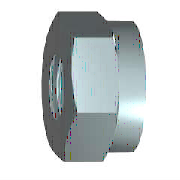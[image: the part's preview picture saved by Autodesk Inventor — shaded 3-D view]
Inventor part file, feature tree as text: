
AUTODESK INVENTOR PART (.ipt)
format: ipt  version: 2015 (Build 190159000, 159)  size: 194,048 bytes
history: native  units: mm (DEFAULTED — no unit token found)
features: sketch x4, extrude x1, chamfer x1, hole x1, other x1, plane x1, fillet x1
ambient origin geometry x7: Origin, YZ Plane, XZ Plane, X Axis, Y Axis, Z Axis, Center Point
bodies: Solid1 (feature_tree), Body (feature_tree)
feature tree (10):
  extrude  "Ring"  Depth=4.4mm
  chamfer  "Chamfer1"  Distance=6.88mm
  hole  "Thread"  [1 undecoded]
  other  "Work Axis1"
  plane  "Work Plane1"
  fillet  "Fillet1"  [1 undecoded]
  sketch  "Sketch1"  dims[d0=9.237604mm d1=4.4mm]
  sketch  "Sketch3"  dims[d3=30.0deg]
  sketch  "Sketch2"  dims[d2=0.0mm]
  sketch  "Sketch4"  dims[d4=30.0deg d5=6.88mm d6=6.88mm d26=90.0deg d7=6.88mm d8=2.4mm d9=0.0mm d30=4.134mm d31=6.0mm d32=4.0mm d33=2.0mm d34=14.3117mm d35=8.0mm d36=20.594885mm d10=0.433013mm d11=30.0deg d12=0.433013mm d13=30.0deg d14=0.0mm d15=0.0mm d45=0.0mm d46=0.433013mm d47=0.433013mm d48=0.0mm d49=0.75mm]
note: 2 required parameter values undecoded (feature->parameter linkage not recoverable at this tier; creation-order binding heuristic only, values carry confidence <= 0.55)
